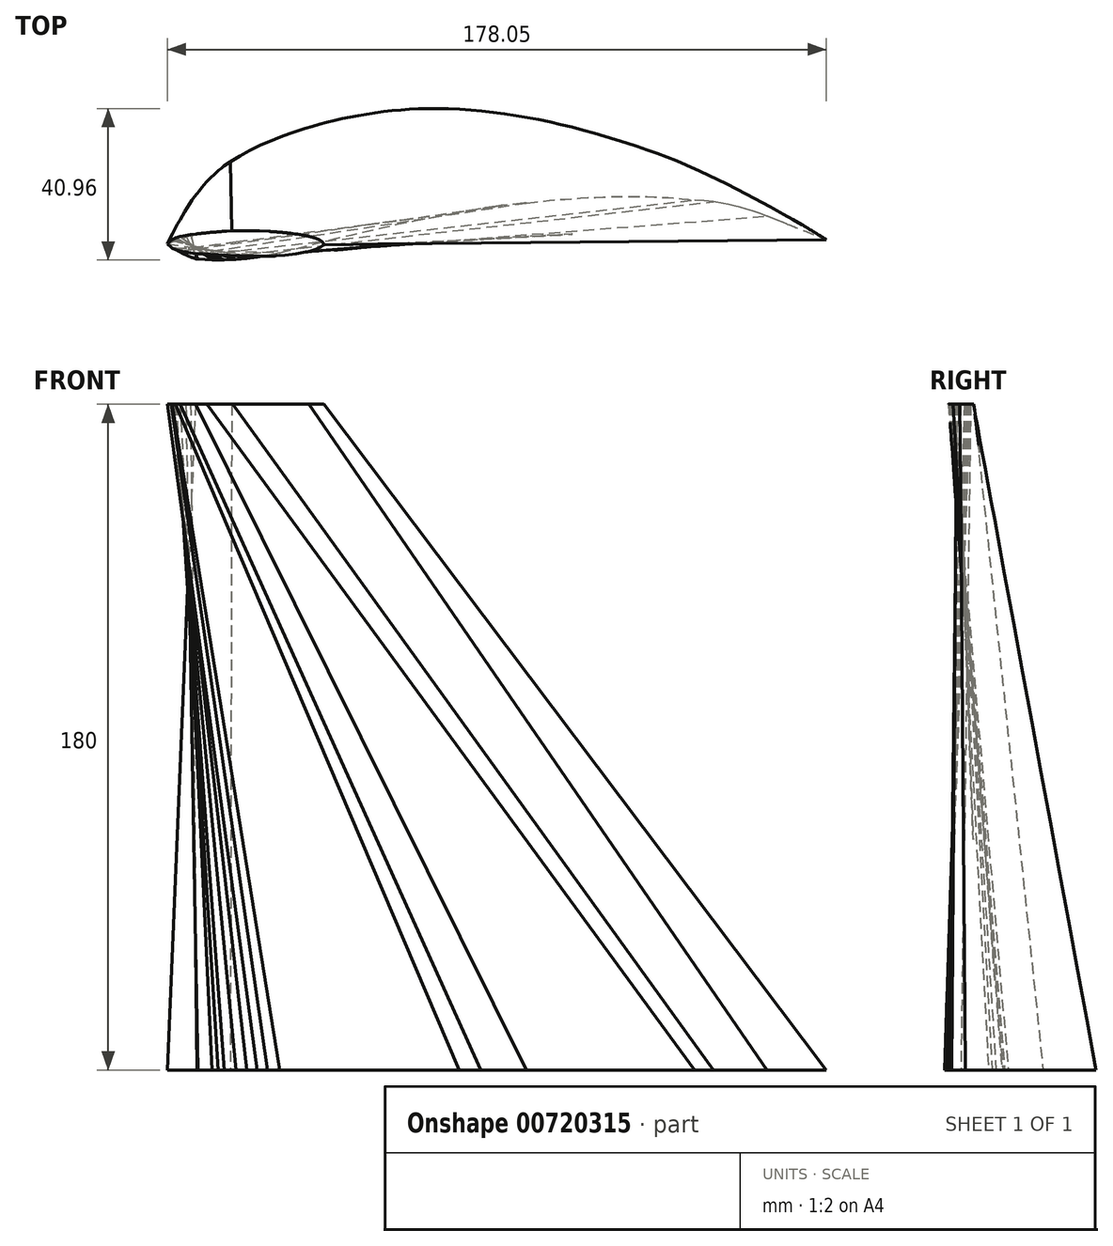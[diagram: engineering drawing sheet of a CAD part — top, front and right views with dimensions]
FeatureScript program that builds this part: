
annotation { "Feature Type Name" : "Feature", "Feature Type Description" : "" }
export const myFeature = defineFeature(function(context is Context, id is Id, definition is map)
    precondition{}
    {
        {
            var Q0;
            Q0=qCreatedBy(makeId("Top.planeOp"),FACE);
            var sketch = newSketch(context, id + "F0", { "sketchPlane" : qUnion([Q0])});
            skLineSegment(sketch, "E0", {"start": v(2.9, 7.22) * mm, "end": v(6.31, 12.13) * mm});
            skLineSegment(sketch, "E1", {"start": v(6.31, 12.13) * mm, "end": v(8.14, 14.47) * mm});
            skLineSegment(sketch, "E2", {"start": v(8.14, 14.47) * mm, "end": v(10.5, 17.07) * mm});
            skLineSegment(sketch, "E3", {"start": v(10.5, 17.07) * mm, "end": v(12.25, 18.7) * mm});
            skLineSegment(sketch, "E4", {"start": v(12.25, 18.7) * mm, "end": v(14.56, 20.54) * mm});
            skLineSegment(sketch, "E5", {"start": v(14.56, 20.54) * mm, "end": v(17.01, 22.23) * mm});
            skLineSegment(sketch, "E6", {"start": v(17.01, 22.23) * mm, "end": v(19.58, 23.77) * mm});
            skLineSegment(sketch, "E7", {"start": v(19.58, 23.77) * mm, "end": v(22.23, 25.2) * mm});
            skLineSegment(sketch, "E8", {"start": v(22.23, 25.2) * mm, "end": v(25.01, 26.57) * mm});
            skLineSegment(sketch, "E9", {"start": v(25.01, 26.57) * mm, "end": v(27.66, 27.78) * mm});
            skLineSegment(sketch, "E10", {"start": v(27.66, 27.78) * mm, "end": v(30.4, 28.95) * mm});
            skLineSegment(sketch, "E11", {"start": v(30.4, 28.95) * mm, "end": v(33.18, 30.03) * mm});
            skLineSegment(sketch, "E12", {"start": v(33.18, 30.03) * mm, "end": v(35.98, 31.03) * mm});
            skLineSegment(sketch, "E13", {"start": v(35.98, 31.03) * mm, "end": v(38.8, 31.95) * mm});
            skLineSegment(sketch, "E14", {"start": v(38.8, 31.95) * mm, "end": v(41.65, 32.78) * mm});
            skLineSegment(sketch, "E15", {"start": v(41.65, 32.78) * mm, "end": v(45.06, 33.66) * mm});
            skLineSegment(sketch, "E16", {"start": v(45.06, 33.66) * mm, "end": v(47.4, 34.19) * mm});
            skLineSegment(sketch, "E17", {"start": v(47.4, 34.19) * mm, "end": v(50.32, 34.76) * mm});
            skLineSegment(sketch, "E18", {"start": v(50.32, 34.76) * mm, "end": v(53.25, 35.25) * mm});
            skLineSegment(sketch, "E19", {"start": v(53.25, 35.25) * mm, "end": v(56.2, 35.66) * mm});
            skLineSegment(sketch, "E20", {"start": v(56.2, 35.66) * mm, "end": v(59.16, 36) * mm});
            skLineSegment(sketch, "E21", {"start": v(59.16, 36) * mm, "end": v(65.1, 36.45) * mm});
            skLineSegment(sketch, "E22", {"start": v(65.1, 36.45) * mm, "end": v(69.08, 36.6) * mm});
            skLineSegment(sketch, "E23", {"start": v(69.08, 36.6) * mm, "end": v(77, 36.55) * mm});
            skLineSegment(sketch, "E24", {"start": v(77, 36.55) * mm, "end": v(82.94, 36.23) * mm});
            skLineSegment(sketch, "E25", {"start": v(82.94, 36.23) * mm, "end": v(88.86, 35.67) * mm});
            skLineSegment(sketch, "E26", {"start": v(88.86, 35.67) * mm, "end": v(94.83, 34.87) * mm});
            skLineSegment(sketch, "E27", {"start": v(94.83, 34.87) * mm, "end": v(100.62, 33.86) * mm});
            skLineSegment(sketch, "E28", {"start": v(100.62, 33.86) * mm, "end": v(106.45, 32.63) * mm});
            skLineSegment(sketch, "E29", {"start": v(106.45, 32.63) * mm, "end": v(112.22, 31.2) * mm});
            skLineSegment(sketch, "E30", {"start": v(112.22, 31.2) * mm, "end": v(120.41, 28.82) * mm});
            skLineSegment(sketch, "E31", {"start": v(120.41, 28.82) * mm, "end": v(123.58, 27.79) * mm});
            skLineSegment(sketch, "E32", {"start": v(123.58, 27.79) * mm, "end": v(129.16, 25.81) * mm});
            skLineSegment(sketch, "E33", {"start": v(129.16, 25.81) * mm, "end": v(134.69, 23.67) * mm});
            skLineSegment(sketch, "E34", {"start": v(134.69, 23.67) * mm, "end": v(140.18, 21.35) * mm});
            skLineSegment(sketch, "E35", {"start": v(140.18, 21.35) * mm, "end": v(143.91, 19.66) * mm});
            skLineSegment(sketch, "E36", {"start": v(143.91, 19.66) * mm, "end": v(151.07, 16.2) * mm});
            skLineSegment(sketch, "E37", {"start": v(151.07, 16.2) * mm, "end": v(156.4, 13.47) * mm});
            skLineSegment(sketch, "E38", {"start": v(156.4, 13.47) * mm, "end": v(162.92, 9.98) * mm});
            skLineSegment(sketch, "E39", {"start": v(162.92, 9.98) * mm, "end": v(166.5, 8.01) * mm});
            skLineSegment(sketch, "E40", {"start": v(166.5, 8.01) * mm, "end": v(168.99, 6.61) * mm});
            skLineSegment(sketch, "E41", {"start": v(168.99, 6.61) * mm, "end": v(171.57, 5.13) * mm});
            skLineSegment(sketch, "E42", {"start": v(171.57, 5.13) * mm, "end": v(174.3, 3.53) * mm});
            skLineSegment(sketch, "E43", {"start": v(174.3, 3.53) * mm, "end": v(175.37, 2.9) * mm});
            skLineSegment(sketch, "E44", {"start": v(175.37, 2.9) * mm, "end": v(176.47, 2.24) * mm});
            skLineSegment(sketch, "E45", {"start": v(176.47, 2.24) * mm, "end": v(177.1, 1.84) * mm});
            skLineSegment(sketch, "E46", {"start": v(177.1, 1.84) * mm, "end": v(177.61, 1.51) * mm});
            skLineSegment(sketch, "E47", {"start": v(177.61, 1.51) * mm, "end": v(177.92, 1.3) * mm});
            skLineSegment(sketch, "E48", {"start": v(177.92, 1.3) * mm, "end": v(178.05, 1.16) * mm});
            skLineSegment(sketch, "E49", {"start": v(178.05, 1.16) * mm, "end": v(178, 1.1) * mm});
            skLineSegment(sketch, "E50", {"start": v(178, 1.1) * mm, "end": v(177.8, 1.14) * mm});
            skLineSegment(sketch, "E51", {"start": v(177.8, 1.14) * mm, "end": v(177.46, 1.25) * mm});
            skLineSegment(sketch, "E52", {"start": v(177.46, 1.25) * mm, "end": v(176.97, 1.42) * mm});
            skLineSegment(sketch, "E53", {"start": v(176.97, 1.42) * mm, "end": v(176.37, 1.65) * mm});
            skLineSegment(sketch, "E54", {"start": v(176.37, 1.65) * mm, "end": v(175.65, 1.94) * mm});
            skLineSegment(sketch, "E55", {"start": v(175.65, 1.94) * mm, "end": v(174.84, 2.27) * mm});
            skLineSegment(sketch, "E56", {"start": v(174.84, 2.27) * mm, "end": v(173.94, 2.65) * mm});
            skLineSegment(sketch, "E57", {"start": v(173.94, 2.65) * mm, "end": v(172.98, 3.05) * mm});
            skLineSegment(sketch, "E58", {"start": v(172.98, 3.05) * mm, "end": v(170.87, 3.94) * mm});
            skLineSegment(sketch, "E59", {"start": v(170.87, 3.94) * mm, "end": v(168.63, 4.88) * mm});
            skLineSegment(sketch, "E60", {"start": v(168.63, 4.88) * mm, "end": v(166.36, 5.8) * mm});
            skLineSegment(sketch, "E61", {"start": v(166.36, 5.8) * mm, "end": v(165, 6.35) * mm});
            skLineSegment(sketch, "E62", {"start": v(165, 6.35) * mm, "end": v(162.06, 7.47) * mm});
            skLineSegment(sketch, "E63", {"start": v(162.06, 7.47) * mm, "end": v(160.09, 8.18) * mm});
            skLineSegment(sketch, "E64", {"start": v(160.09, 8.18) * mm, "end": v(158.22, 8.8) * mm});
            skLineSegment(sketch, "E65", {"start": v(158.22, 8.8) * mm, "end": v(156.46, 9.36) * mm});
            skLineSegment(sketch, "E66", {"start": v(156.46, 9.36) * mm, "end": v(154.78, 9.84) * mm});
            skLineSegment(sketch, "E67", {"start": v(154.78, 9.84) * mm, "end": v(153.2, 10.26) * mm});
            skLineSegment(sketch, "E68", {"start": v(153.2, 10.26) * mm, "end": v(151.68, 10.61) * mm});
            skLineSegment(sketch, "E69", {"start": v(151.68, 10.61) * mm, "end": v(150.23, 10.92) * mm});
            skLineSegment(sketch, "E70", {"start": v(150.23, 10.92) * mm, "end": v(147.52, 11.37) * mm});
            skLineSegment(sketch, "E71", {"start": v(147.52, 11.37) * mm, "end": v(144.98, 11.65) * mm});
            skLineSegment(sketch, "E72", {"start": v(144.98, 11.65) * mm, "end": v(142.55, 11.81) * mm});
            skLineSegment(sketch, "E73", {"start": v(142.55, 11.81) * mm, "end": v(137.79, 11.89) * mm});
            skLineSegment(sketch, "E74", {"start": v(137.79, 11.89) * mm, "end": v(135.8, 11.88) * mm});
            skLineSegment(sketch, "E75", {"start": v(135.8, 11.88) * mm, "end": v(132.74, 11.89) * mm});
            skLineSegment(sketch, "E76", {"start": v(132.74, 11.89) * mm, "end": v(130.04, 11.9) * mm});
            skLineSegment(sketch, "E77", {"start": v(130.04, 11.9) * mm, "end": v(127.24, 11.92) * mm});
            skLineSegment(sketch, "E78", {"start": v(127.24, 11.92) * mm, "end": v(121.4, 11.93) * mm});
            skLineSegment(sketch, "E79", {"start": v(121.4, 11.93) * mm, "end": v(115.32, 11.9) * mm});
            skLineSegment(sketch, "E80", {"start": v(115.32, 11.9) * mm, "end": v(109.1, 11.77) * mm});
            skLineSegment(sketch, "E81", {"start": v(109.1, 11.77) * mm, "end": v(102.83, 11.5) * mm});
            skLineSegment(sketch, "E82", {"start": v(102.83, 11.5) * mm, "end": v(96.39, 11.02) * mm});
            skLineSegment(sketch, "E83", {"start": v(96.39, 11.02) * mm, "end": v(90.6, 10.38) * mm});
            skLineSegment(sketch, "E84", {"start": v(90.6, 10.38) * mm, "end": v(84.68, 9.51) * mm});
            skLineSegment(sketch, "E85", {"start": v(84.68, 9.51) * mm, "end": v(78.86, 8.49) * mm});
            skLineSegment(sketch, "E86", {"start": v(78.86, 8.49) * mm, "end": v(73.1, 7.32) * mm});
            skLineSegment(sketch, "E87", {"start": v(73.1, 7.32) * mm, "end": v(67.35, 6.05) * mm});
            skLineSegment(sketch, "E88", {"start": v(67.35, 6.05) * mm, "end": v(59.06, 4.1) * mm});
            skLineSegment(sketch, "E89", {"start": v(59.06, 4.1) * mm, "end": v(49.82, 1.9) * mm});
            skLineSegment(sketch, "E90", {"start": v(49.82, 1.9) * mm, "end": v(43.94, 0.53) * mm});
            skLineSegment(sketch, "E91", {"start": v(43.94, 0.53) * mm, "end": v(38.14, -0.8) * mm});
            skLineSegment(sketch, "E92", {"start": v(38.14, -0.8) * mm, "end": v(30.37, -2.46) * mm});
            skLineSegment(sketch, "E93", {"start": v(30.37, -2.46) * mm, "end": v(27.03, -3.11) * mm});
            skLineSegment(sketch, "E94", {"start": v(27.03, -3.11) * mm, "end": v(24.3, -3.57) * mm});
            skLineSegment(sketch, "E95", {"start": v(24.3, -3.57) * mm, "end": v(21.5, -3.95) * mm});
            skLineSegment(sketch, "E96", {"start": v(21.5, -3.95) * mm, "end": v(18.54, -4.22) * mm});
            skLineSegment(sketch, "E97", {"start": v(18.54, -4.22) * mm, "end": v(15.38, -4.37) * mm});
            skLineSegment(sketch, "E98", {"start": v(15.38, -4.37) * mm, "end": v(13.7, -4.38) * mm});
            skLineSegment(sketch, "E99", {"start": v(13.7, -4.38) * mm, "end": v(12.05, -4.36) * mm});
            skLineSegment(sketch, "E100", {"start": v(12.05, -4.36) * mm, "end": v(8.27, -4.16) * mm});
            skLineSegment(sketch, "E101", {"start": v(8.27, -4.16) * mm, "end": v(6.47, -3.95) * mm});
            skLineSegment(sketch, "E102", {"start": v(6.47, -3.95) * mm, "end": v(4.77, -3.64) * mm});
            skLineSegment(sketch, "E103", {"start": v(4.77, -3.64) * mm, "end": v(3.24, -3.22) * mm});
            skLineSegment(sketch, "E104", {"start": v(3.24, -3.22) * mm, "end": v(1.94, -2.66) * mm});
            skLineSegment(sketch, "E105", {"start": v(1.94, -2.66) * mm, "end": v(1.4, -2.32) * mm});
            skLineSegment(sketch, "E106", {"start": v(1.4, -2.32) * mm, "end": v(0.92, -1.95) * mm});
            skLineSegment(sketch, "E107", {"start": v(0.92, -1.95) * mm, "end": v(0.54, -1.53) * mm});
            skLineSegment(sketch, "E108", {"start": v(0.54, -1.53) * mm, "end": v(0.26, -1.07) * mm});
            skLineSegment(sketch, "E109", {"start": v(0.26, -1.07) * mm, "end": v(0.13, -0.73) * mm});
            skLineSegment(sketch, "E110", {"start": v(0.13, -0.73) * mm, "end": v(0, 0) * mm});
            skLineSegment(sketch, "E111", {"start": v(0, 0) * mm, "end": v(0.02, 0.6) * mm});
            skLineSegment(sketch, "E112", {"start": v(0.02, 0.6) * mm, "end": v(0.12, 1.24) * mm});
            skLineSegment(sketch, "E113", {"start": v(0.12, 1.24) * mm, "end": v(0.55, 2.61) * mm});
            skLineSegment(sketch, "E114", {"start": v(0.55, 2.61) * mm, "end": v(1.2, 4.1) * mm});
            skLineSegment(sketch, "E115", {"start": v(1.2, 4.1) * mm, "end": v(2, 5.64) * mm});
            skLineSegment(sketch, "E116", {"start": v(2, 5.64) * mm, "end": v(2.9, 7.22) * mm});
            skSolve(sketch);
        }
        {
            var Q0;
            Q0=qCreatedBy(makeId("Top.planeOp"),FACE);
            cPlane(context, id + "F1", {"entities" : qUnion([Q0]), "cplaneType" : CPlaneType.OFFSET, "offset" : 180 * mm, "width" : 152.4 * mm, "height" : 152.4 * mm});
        }
        {
            var Q0;
            Q0=qCreatedBy(id+"F1.planeOp",FACE);
            var sketch = newSketch(context, id + "F2", { "sketchPlane" : qUnion([Q0])});
            skLineSegment(sketch, "E117", {"start": v(0, 0) * mm, "end": v(1, 0.95) * mm});
            skLineSegment(sketch, "E118", {"start": v(1, 0.95) * mm, "end": v(1.3, 1.17) * mm});
            skLineSegment(sketch, "E119", {"start": v(1.3, 1.17) * mm, "end": v(2.15, 1.62) * mm});
            skLineSegment(sketch, "E120", {"start": v(2.15, 1.62) * mm, "end": v(3.47, 2) * mm});
            skLineSegment(sketch, "E121", {"start": v(3.47, 2) * mm, "end": v(4.97, 2.25) * mm});
            skLineSegment(sketch, "E122", {"start": v(4.97, 2.25) * mm, "end": v(7.58, 2.65) * mm});
            skLineSegment(sketch, "E123", {"start": v(7.58, 2.65) * mm, "end": v(10.6, 3.05) * mm});
            skLineSegment(sketch, "E124", {"start": v(10.6, 3.05) * mm, "end": v(12.97, 3.26) * mm});
            skLineSegment(sketch, "E125", {"start": v(12.97, 3.26) * mm, "end": v(17.49, 3.46) * mm});
            skLineSegment(sketch, "E126", {"start": v(17.49, 3.46) * mm, "end": v(21.17, 3.51) * mm});
            skLineSegment(sketch, "E127", {"start": v(21.17, 3.51) * mm, "end": v(24.84, 3.46) * mm});
            skLineSegment(sketch, "E128", {"start": v(24.84, 3.46) * mm, "end": v(29.33, 3.26) * mm});
            skLineSegment(sketch, "E129", {"start": v(29.33, 3.26) * mm, "end": v(31.72, 3.05) * mm});
            skLineSegment(sketch, "E130", {"start": v(31.72, 3.05) * mm, "end": v(34.82, 2.65) * mm});
            skLineSegment(sketch, "E131", {"start": v(34.82, 2.65) * mm, "end": v(37.36, 2.25) * mm});
            skLineSegment(sketch, "E132", {"start": v(37.36, 2.25) * mm, "end": v(38.72, 2) * mm});
            skLineSegment(sketch, "E133", {"start": v(38.72, 2) * mm, "end": v(40.02, 1.62) * mm});
            skLineSegment(sketch, "E134", {"start": v(40.02, 1.62) * mm, "end": v(41.03, 1.17) * mm});
            skLineSegment(sketch, "E135", {"start": v(41.03, 1.17) * mm, "end": v(41.44, 0.95) * mm});
            skLineSegment(sketch, "E136", {"start": v(41.44, 0.95) * mm, "end": v(42.06, 0.5) * mm});
            skLineSegment(sketch, "E137", {"start": v(42.06, 0.5) * mm, "end": v(42.25, 0.25) * mm});
            skLineSegment(sketch, "E138", {"start": v(42.25, 0.25) * mm, "end": v(42.33, 0) * mm});
            skLineSegment(sketch, "E139", {"start": v(42.33, 0) * mm, "end": v(42.25, -0.25) * mm});
            skLineSegment(sketch, "E140", {"start": v(42.25, -0.25) * mm, "end": v(42.06, -0.5) * mm});
            skLineSegment(sketch, "E141", {"start": v(42.06, -0.5) * mm, "end": v(41.44, -0.95) * mm});
            skLineSegment(sketch, "E142", {"start": v(41.44, -0.95) * mm, "end": v(41.03, -1.17) * mm});
            skLineSegment(sketch, "E143", {"start": v(41.03, -1.17) * mm, "end": v(40.02, -1.62) * mm});
            skLineSegment(sketch, "E144", {"start": v(40.02, -1.62) * mm, "end": v(38.72, -2) * mm});
            skLineSegment(sketch, "E145", {"start": v(38.72, -2) * mm, "end": v(37.36, -2.25) * mm});
            skLineSegment(sketch, "E146", {"start": v(37.36, -2.25) * mm, "end": v(34.82, -2.65) * mm});
            skLineSegment(sketch, "E147", {"start": v(34.82, -2.65) * mm, "end": v(31.72, -3.05) * mm});
            skLineSegment(sketch, "E148", {"start": v(31.72, -3.05) * mm, "end": v(29.33, -3.26) * mm});
            skLineSegment(sketch, "E149", {"start": v(29.33, -3.26) * mm, "end": v(24.84, -3.46) * mm});
            skLineSegment(sketch, "E150", {"start": v(24.84, -3.46) * mm, "end": v(21.17, -3.51) * mm});
            skLineSegment(sketch, "E151", {"start": v(21.17, -3.51) * mm, "end": v(17.49, -3.46) * mm});
            skLineSegment(sketch, "E152", {"start": v(17.49, -3.46) * mm, "end": v(12.97, -3.26) * mm});
            skLineSegment(sketch, "E153", {"start": v(12.97, -3.26) * mm, "end": v(10.6, -3.05) * mm});
            skLineSegment(sketch, "E154", {"start": v(10.6, -3.05) * mm, "end": v(7.58, -2.65) * mm});
            skLineSegment(sketch, "E155", {"start": v(7.58, -2.65) * mm, "end": v(4.97, -2.25) * mm});
            skLineSegment(sketch, "E156", {"start": v(4.97, -2.25) * mm, "end": v(3.47, -2) * mm});
            skLineSegment(sketch, "E157", {"start": v(3.47, -2) * mm, "end": v(2.15, -1.62) * mm});
            skLineSegment(sketch, "E158", {"start": v(2.15, -1.62) * mm, "end": v(1.3, -1.17) * mm});
            skLineSegment(sketch, "E159", {"start": v(1.3, -1.17) * mm, "end": v(1, -0.95) * mm});
            skLineSegment(sketch, "E160", {"start": v(1, -0.95) * mm, "end": v(0, 0) * mm});
            skSolve(sketch);
        }
        {
            var Q0;
            Q0=makeQuery(id+"F0.imprint","IMPRINT",FACE,{"disambiguationData":[TD([[makeQuery(id+"F0.imprint","IMPRINT",EDGE,{"derivedFrom":sQuery(id+"F0.wireOp",EDGE,"E0")}),-1.0]])]});
            var sketch = newSketch(context, id + "F3", { "sketchPlane" : qUnion([Q0])});
            skPoint(sketch, "E161.0", {"position": v(0, 0) * mm});
            skPoint(sketch, "E161.1", {"position": v(25.01, 26.57) * mm});
            skPoint(sketch, "E161.2", {"position": v(140.18, 21.35) * mm});
            skPoint(sketch, "E161.3", {"position": v(178.05, 1.16) * mm});
            skPoint(sketch, "E161.4", {"position": v(142.55, 11.81) * mm});
            skPoint(sketch, "E161.5", {"position": v(78.86, 8.49) * mm});
            skPoint(sketch, "E161.6", {"position": v(30.37, -2.46) * mm});
            skPoint(sketch, "E161.7", {"position": v(73.04, 36.58) * mm});
            skFitSpline(sketch, "E162", {"points": [v(0, 0) * mm, v(25.01, 26.57) * mm, v(73.04, 36.58) * mm, v(140.18, 21.35) * mm, v(178.05, 1.16) * mm], "startDerivative": vector(114.36, 235.38) * mm, "endDerivative": vector(144.81, -89.54) * mm});
            skFitSpline(sketch, "E163", {"points": [v(0, 0) * mm, v(30.37, -2.46) * mm, v(78.86, 8.49) * mm, v(142.55, 11.81) * mm, v(178.05, 1.16) * mm], "startDerivative": vector(151.63, -111.35) * mm, "endDerivative": vector(140.67, -57.19) * mm});
            skSolve(sketch);
        }
        {
            var Q0;
            Q0=makeQuery(id+"F2.imprint","IMPRINT",FACE,{"disambiguationData":[TD([[makeQuery(id+"F2.imprint","IMPRINT",EDGE,{"derivedFrom":sQuery(id+"F2.wireOp",EDGE,"E117")}),-1.0]])]});
            var sketch = newSketch(context, id + "F4", { "sketchPlane" : qUnion([Q0])});
            skPoint(sketch, "E164.0", {"position": v(0, 0) * mm});
            skPoint(sketch, "E164.1", {"position": v(7.58, 2.65) * mm});
            skPoint(sketch, "E164.2", {"position": v(24.84, 3.46) * mm});
            skPoint(sketch, "E164.3", {"position": v(42.25, -0.25) * mm});
            skPoint(sketch, "E164.4", {"position": v(29.33, -3.26) * mm});
            skPoint(sketch, "E164.5", {"position": v(7.58, -2.65) * mm});
            skFitSpline(sketch, "E165", {"points": [v(0, 0) * mm, v(7.58, 2.65) * mm, v(24.84, 3.46) * mm, v(42.25, -0.25) * mm], "startDerivative": vector(15.4, 22.81) * mm, "endDerivative": vector(0.28, -18.96) * mm});
            skFitSpline(sketch, "E166", {"points": [v(0, 0) * mm, v(7.58, -2.65) * mm, v(29.33, -3.26) * mm, v(42.25, -0.25) * mm], "startDerivative": vector(18.78, -27.84) * mm, "endDerivative": vector(18.96, 17) * mm});
            skSolve(sketch);
        }
        {
            var Q0;
            Q0=makeQuery(id+"F4.imprint","IMPRINT",FACE,{"disambiguationData":[TD([[makeQuery(id+"F4.imprint","IMPRINT",EDGE,{"derivedFrom":makeQuery(id+"F2.imprint","IMPRINT",EDGE,{"derivedFrom":sQuery(id+"F2.wireOp",EDGE,"E117")})}),-1.0]])]});
            var Q1;
            {var subQ24=makeQuery(id+"F0.imprint","IMPRINT",EDGE,{"derivedFrom":sQuery(id+"F0.wireOp",EDGE,"E6")});Q1=makeQuery(id+"F3.imprint","IMPRINT",FACE,{"disambiguationData":[TD([[makeQuery(id+"F3.imprint","IMPRINT",EDGE,{"derivedFrom":subQ24}),-1.0]])]});}
            var Q2;
            Q2=sQuery(id+"F4.wireOp",VERTEX,"E164.3");
            var Q3;
            Q3=sQuery(id+"F3.wireOp",VERTEX,"E161.3");
            loft(context, id + "F5", {"sheetProfilesArray" : [{ "sheetProfileEntities" : qUnion([Q0]) }, { "sheetProfileEntities" : qUnion([Q1]) }], "matchConnections" : true, "connections" : [{ "connectionEntities" : qUnion([Q2, Q3]), "connectionEdgeQueries" : qUnion([]), "connectionEdgeParameters" : [] }]});
        }
    });
